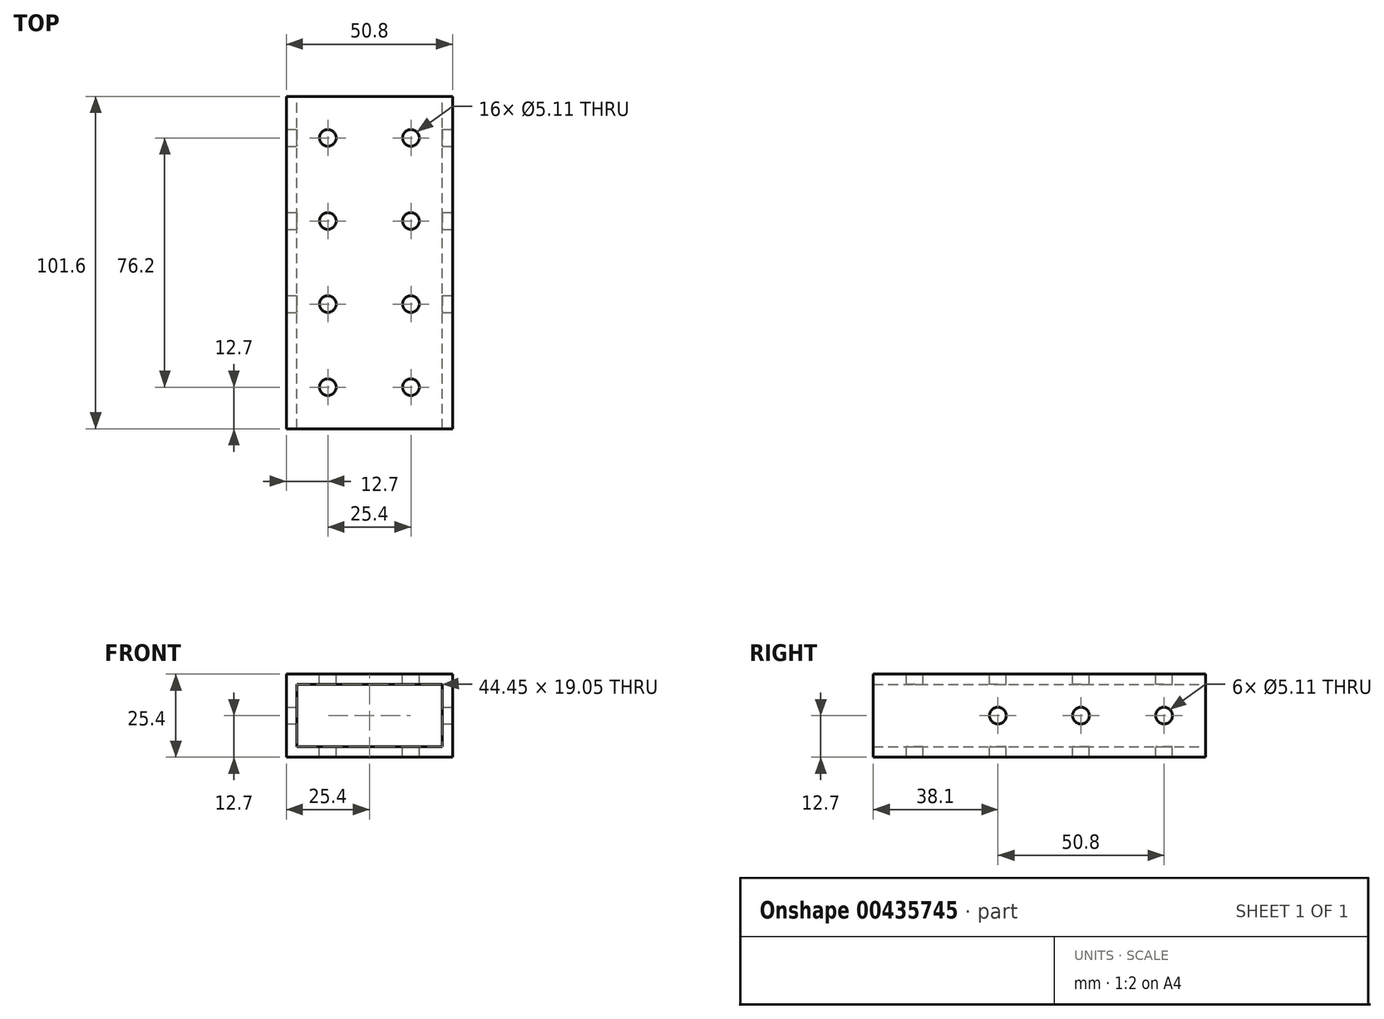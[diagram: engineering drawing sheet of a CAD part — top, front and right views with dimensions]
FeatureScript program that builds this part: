
annotation { "Feature Type Name" : "Feature", "Feature Type Description" : "" }
export const myFeature = defineFeature(function(context is Context, id is Id, definition is map)
    precondition{}
    {
        {
            var Q0;
            Q0=qCreatedBy(makeId("Front.planeOp"),FACE);
            var sketch = newSketch(context, id + "F0", { "sketchPlane" : qUnion([Q0])});
            skLineSegment(sketch, "E0.bottom", {"start": v(25.4, 12.7) * mm, "end": v(-25.4, 12.7) * mm});
            skLineSegment(sketch, "E0.top", {"start": v(25.4, -12.7) * mm, "end": v(-25.4, -12.7) * mm});
            skLineSegment(sketch, "E0.left", {"start": v(25.4, 12.7) * mm, "end": v(25.4, -12.7) * mm});
            skLineSegment(sketch, "E0.right", {"start": v(-25.4, 12.7) * mm, "end": v(-25.4, -12.7) * mm});
            skPoint(sketch, "E0.middle", {"position": v(0, 0) * mm});
            skLineSegment(sketch, "E1.bottom", {"start": v(22.22, 9.53) * mm, "end": v(-22.23, 9.52) * mm});
            skLineSegment(sketch, "E1.top", {"start": v(22.22, -9.52) * mm, "end": v(-22.23, -9.52) * mm});
            skLineSegment(sketch, "E1.left", {"start": v(22.23, 9.53) * mm, "end": v(22.23, -9.52) * mm});
            skLineSegment(sketch, "E1.right", {"start": v(-22.23, 9.52) * mm, "end": v(-22.23, -9.53) * mm});
            skSolve(sketch);
        }
        {
            var Q0;
            Q0=makeQuery(id+"F0.imprint","IMPRINT",FACE,{"disambiguationData":[TD([[makeQuery(id+"F0.imprint","IMPRINT",EDGE,{"derivedFrom":sQuery(id+"F0.wireOp",EDGE,"E0.bottom")}),1.0]])]});
            extrude(context, id + "F1", {"entities" : qUnion([Q0]), "depth" : 101.6 * mm});
        }
        {
            var Q0;
            Q0=makeQuery(id+"F1.opExtrude","SWEPT_FACE",FACE,{"disambiguationData":[OSD([sQuery(id+"F0.wireOp",EDGE,"E0.bottom")])]});
            var sketch = newSketch(context, id + "F2", { "sketchPlane" : qUnion([Q0])});
            skCircle(sketch, "E2", {"center": v(-12.7, -12.7) * mm, "radius": 4.59 * mm});
            skCircle(sketch, "E3.0.1.0", {"center": v(-12.7, -38.1) * mm, "radius": 4.59 * mm});
            skCircle(sketch, "E3.0.2.0", {"center": v(-12.7, -63.5) * mm, "radius": 4.59 * mm});
            skCircle(sketch, "E3.0.3.0", {"center": v(-12.7, -88.9) * mm, "radius": 4.59 * mm});
            skCircle(sketch, "E3.1.0.0", {"center": v(12.7, -12.7) * mm, "radius": 4.59 * mm});
            skCircle(sketch, "E3.1.1.0", {"center": v(12.7, -38.1) * mm, "radius": 4.59 * mm});
            skCircle(sketch, "E3.1.2.0", {"center": v(12.7, -63.5) * mm, "radius": 4.59 * mm});
            skCircle(sketch, "E3.1.3.0", {"center": v(12.7, -88.9) * mm, "radius": 4.59 * mm});
            skLineSegment(sketch, "E3.direction1", {"start": v(-12.7, -12.7) * mm, "end": v(12.7, -12.7) * mm, "construction": true});
            skLineSegment(sketch, "E3.direction2", {"start": v(-12.7, -12.7) * mm, "end": v(-12.7, -38.1) * mm, "construction": true});
            skSolve(sketch);
        }
        {
            var Q0;
            Q0=sQuery(id+"F2.wireOp",VERTEX,"E3.0.3.0.center");
            var Q1;
            Q1=sQuery(id+"F2.wireOp",VERTEX,"E2.center");
            var Q2;
            Q2=sQuery(id+"F2.wireOp",VERTEX,"E3.0.1.0.center");
            var Q3;
            Q3=sQuery(id+"F2.wireOp",VERTEX,"E3.0.2.0.center");
            var Q4;
            Q4=sQuery(id+"F2.wireOp",VERTEX,"E3.direction1.end");
            var Q5;
            Q5=sQuery(id+"F2.wireOp",VERTEX,"E3.1.3.0.center");
            var Q6;
            Q6=sQuery(id+"F2.wireOp",VERTEX,"E3.1.1.0.center");
            var Q7;
            Q7=sQuery(id+"F2.wireOp",VERTEX,"E3.1.2.0.center");
            var Q8;
            Q8=makeQuery(id+"F1.opExtrude","SWEPT_BODY",BODY,{"disambiguationData":[OSD([sQuery(id+"F0.wireOp",EDGE,"E0.bottom"),sQuery(id+"F0.wireOp",EDGE,"E0.top"),sQuery(id+"F0.wireOp",EDGE,"E0.left"),sQuery(id+"F0.wireOp",EDGE,"E0.right"),sQuery(id+"F0.wireOp",EDGE,"E1.bottom"),sQuery(id+"F0.wireOp",EDGE,"E1.top"),sQuery(id+"F0.wireOp",EDGE,"E1.left"),sQuery(id+"F0.wireOp",EDGE,"E1.right")])]});
            hole(context, id + "F3", {"style" : HoleStyle.SIMPLE, "endStyle" : HoleEndStyle.THROUGH, "holeDiameter" : 5.1 * mm, "isTappedThrough" : true, "tappedDepth" : 12.7 * mm, "tapClearance" : 3, "locations" : qUnion([Q0, Q1, Q2, Q3, Q4, Q5, Q6, Q7]), "scope" : qUnion([Q8])});
        }
        {
            var Q0;
            Q0=makeQuery(id+"F1.opExtrude","SWEPT_FACE",FACE,{"disambiguationData":[OSD([sQuery(id+"F0.wireOp",EDGE,"E0.left")])]});
            var sketch = newSketch(context, id + "F4", { "sketchPlane" : qUnion([Q0])});
            skCircle(sketch, "E4", {"center": v(-88.9, 0) * mm, "radius": 2.55 * mm});
            skCircle(sketch, "E5.1.0.0", {"center": v(-63.5, 0) * mm, "radius": 2.55 * mm});
            skCircle(sketch, "E5.1.1.0", {"center": v(-63.5, 0) * mm, "radius": 2.55 * mm});
            skCircle(sketch, "E5.2.0.0", {"center": v(-38.1, 0) * mm, "radius": 2.55 * mm});
            skCircle(sketch, "E5.2.1.0", {"center": v(-38.1, 0) * mm, "radius": 2.55 * mm});
            skCircle(sketch, "E5.3.0.0", {"center": v(-12.7, 0) * mm, "radius": 2.55 * mm});
            skCircle(sketch, "E5.3.1.0", {"center": v(-12.7, 0) * mm, "radius": 2.55 * mm});
            skLineSegment(sketch, "E5.direction1", {"start": v(-88.9, 0) * mm, "end": v(-63.5, 0) * mm, "construction": true});
            skLineSegment(sketch, "E5.direction2", {"start": v(-88.9, 0) * mm, "end": v(-88.9, 0) * mm});
            skSolve(sketch);
        }
        {
            var Q0;
            Q0=sQuery(id+"F4.wireOp",VERTEX,"E5.6.1.0.center");
            var Q1;
            Q1=sQuery(id+"F4.wireOp",VERTEX,"E4.center");
            var Q2;
            Q2=sQuery(id+"F4.wireOp",VERTEX,"E5.1.1.0.center");
            var Q3;
            Q3=sQuery(id+"F4.wireOp",VERTEX,"E5.2.1.0.center");
            var Q4;
            Q4=sQuery(id+"F4.wireOp",VERTEX,"E5.3.1.0.center");
            var Q5;
            Q5=sQuery(id+"F4.wireOp",VERTEX,"E5.4.0.0.center");
            var Q6;
            Q6=sQuery(id+"F4.wireOp",VERTEX,"E5.5.1.0.center");
            var Q7;
            Q7=makeQuery(id+"F1.opExtrude","SWEPT_BODY",BODY,{"disambiguationData":[OSD([sQuery(id+"F0.wireOp",EDGE,"E0.bottom"),sQuery(id+"F0.wireOp",EDGE,"E0.top"),sQuery(id+"F0.wireOp",EDGE,"E0.left"),sQuery(id+"F0.wireOp",EDGE,"E0.right"),sQuery(id+"F0.wireOp",EDGE,"E1.bottom"),sQuery(id+"F0.wireOp",EDGE,"E1.top"),sQuery(id+"F0.wireOp",EDGE,"E1.left"),sQuery(id+"F0.wireOp",EDGE,"E1.right")])]});
            hole(context, id + "F5", {"style" : HoleStyle.SIMPLE, "endStyle" : HoleEndStyle.THROUGH, "holeDiameter" : 5.1 * mm, "isTappedThrough" : true, "tappedDepth" : 12.7 * mm, "tapClearance" : 3, "locations" : qUnion([Q0, Q1, Q2, Q3, Q4, Q5, Q6]), "scope" : qUnion([Q7])});
        }
    });
